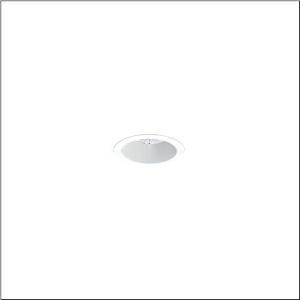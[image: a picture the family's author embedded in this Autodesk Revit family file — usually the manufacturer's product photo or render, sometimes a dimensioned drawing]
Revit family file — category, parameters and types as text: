
# Revit family: lunis_21_s_51db18ma91c
name_source: partatom
category: Lighting Fixtures
units: mm (PartAtom-declared; Revit-internal decimal feet)

## family parameters
Cut with Voids When Loaded = No
Host = Face
Light Source = No
Part Type = Normal
Room Calculation Point = No
Round Connector Dimension = Use Diameter
Shared = No

## types (1)
- --- (1 x LED, 970 lm, 5.9 W, 6500K)
    Apparent Load = 6 VA
    CIE Flux Codes = 86 95 99 100 100
    Color Rendering = 80
    Color Temperature = 6500K
    Default Elevation = 1800 mm
    Description = Lunis 21,  S, downlight, light control with lens, of PMMA, anti glare with reflector, of PC, light emission: direct distribution, LED rated luminous flux: 980lm, light colour: 830/840/865, with terminal, 3-pole, mains connection: 220..240V, AC, 50..60Hz, housing, round, of diecast aluminium, traffic white (RAL 9016), diameter: 84mm, clamping range: 1..40mm, protection rating (complete): IP20, protection rating (on room side): IP54, insulation class (complete): insulation class II (safety insulation), certification: CE, impact resistance: IK03, packaging unit: 1 piece
    Height = 0 mm  [stored 0 ft]
    Lamp = 1 x LED
    Lamp Light Flux = 970 lm
    Lamp Power = 5.9 W
    Lamp count = 1
    Length = 84 mm
    Luminous efficacy = 164 lm/W
    Manufacturer = Siteco
    ModVariant = No
    Model = 51DB18MA91C
    Mounting Place = Ceiling
    Mounting Type = Recessed
    Number of Poles = 1
    OnlyDefault = Yes
    Power Factor = 1
    Product Name = Lunis 21 S
    Product group = downlight
    ProductGroupID = 400
    Protection Class = Protection class II
    Protection Degree = IP 20
    RLX_Detail_Level = 1
    RLX_Emergency_Light_Flux = 0 lm
    RLX_Emergency_Type = 0
    RLX_Emergency_Type_DB = No
    RlxData = <blob elided: 7849 chars, md5=60524f56>
    Socket = socket
    Standby Power = 0 W
    System Light Flux = 970 lm
    System Power = 6 W
    Type Comments = individual setting: colour temperature 6500K
    Type Image = l_1290842.jpg
    URL = http://relux.com
    VarID = @adj_019718
    Voltage = 0 V
    Weight = 0.00 kg
    Width = 0 mm  [stored 0 ft]

note: [stored X ft] marks values corroborated as IEEE doubles in the binary element streams (Revit-internal decimal feet)

## geometry (parser evidence)
native form markers: Sweep x9
no freeform markers — native parametric forms only
